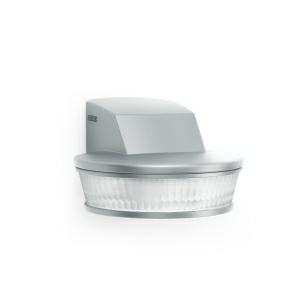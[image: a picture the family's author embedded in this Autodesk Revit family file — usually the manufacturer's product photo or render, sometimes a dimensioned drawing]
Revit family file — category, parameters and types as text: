
# Revit family: sensiq_s_034962
name_source: partatom
category: Elektroinstallationen
revit_build: Autodesk Revit 2016 (Build: 20190508_0715(x64)
units: mm (PartAtom-declared; Revit-internal decimal feet)

## family parameters
Basisbauteil = Fläche
Beim Laden mit Abzugskörper schneiden = Nein
Bemaßung runder Anschluss = Durchmesser verwenden
Beschriftungsausrichtung beibehalten = Nein
Gemeinsam genutzt = Nein
Raumberechnungspunkt = Nein
Teiletyp = Normal

## types (1)
- sensIQ S
    Apparent Load = 0 VA
    Beschreibung = Type: Motion detectors; Type of accessory: Corner adapter; Dimensions (L x W x H): 128 x 114 x 74 mm; Mains power supply: 100 – 240 V / 50 – 60 Hz; Power supply, detail: 500 VA max., 120 V; Sensor Technology: passive infrared; Application, place: Indoors, Outdoors; Application, room: multi-storey / underground car park, outdoors, warehouse, front door, all round the building, courtyard & driveway, Indoors; Installation site: wall, corner; Installation: Surface wiring; Switching zones: 1360 switching zones; Electronic scalability: No; Mechanical scalability: Yes; Mounting height: 2,00 – 5,00 m; Optimum mounting height: 2 m; Detection angle: 300 °; Angle of aperture: 90 °; Sneak-by guard: Yes; Capability of masking out individual segments: Yes; Reach, detail: Reach adjustable from 2 - 20 m in 3 directions (100° in each); Reach, radial: r = 4 m (42 m²); Reach, tangential: r = 20 m (1047 m²); Twilight setting TEACH: Yes; Twilight setting: 2 – 2000 lx; Time setting: 5 sec – 15 min; Switching output 1, resistive: 2000 W; Constant-lighting control: No; Basic light level function: No; Functions: Normal / test mode, Manual ON / ON-OFF; Settings via: Remote control, Potentiometers, Smart Remote; With remote control: Yes; Interconnection: Yes; IP-rating: IP54; Material: Plastic; Ambient temperature: -20 – 50 °C; Colour: Silver; IDs, certificates: VDE; Manufacturer's Warranty: 5 years; Version: inox; PU1, EAN: 4007841034962
    Height = 74 mm
    Hersteller = Steinel
    Length = 128 mm
    Maximum range = 22.149 m
    ModVariant = Nein
    Modell = 034962
    Mounting Type = Surface mounted
    Number of Poles = 1
    OnlyDefault = Ja
    Power Factor = 1
    Product Name = sensIQ S
    Product group = Sensor-switched indoor light
    ProductGroupID = 30
    Protection Class = Protection class
    Protection Degree = IP 54
    RlxData = <blob elided: 170617 chars, md5=7da0c219>
    Sensor characteristics = Semi circular 145°-300°
    Sensor type = Passive (infrared)
    SensorDataFile = <blob elided: 9086 chars, md5=cfd8d4b9>
    Type of entry = Motion
    Typenbild = produkt1_034962.jpg
    Typenkommentare = Product without accessories
    URL = http://relux.com
    VarID = ---
    Voltage = 0 V
    Vorgabe-Ansicht = 1800 mm
    Weight = 0.00 kg
    Width = 114 mm

## geometry (parser evidence)
native form markers: Sweep x19
no freeform markers — native parametric forms only
